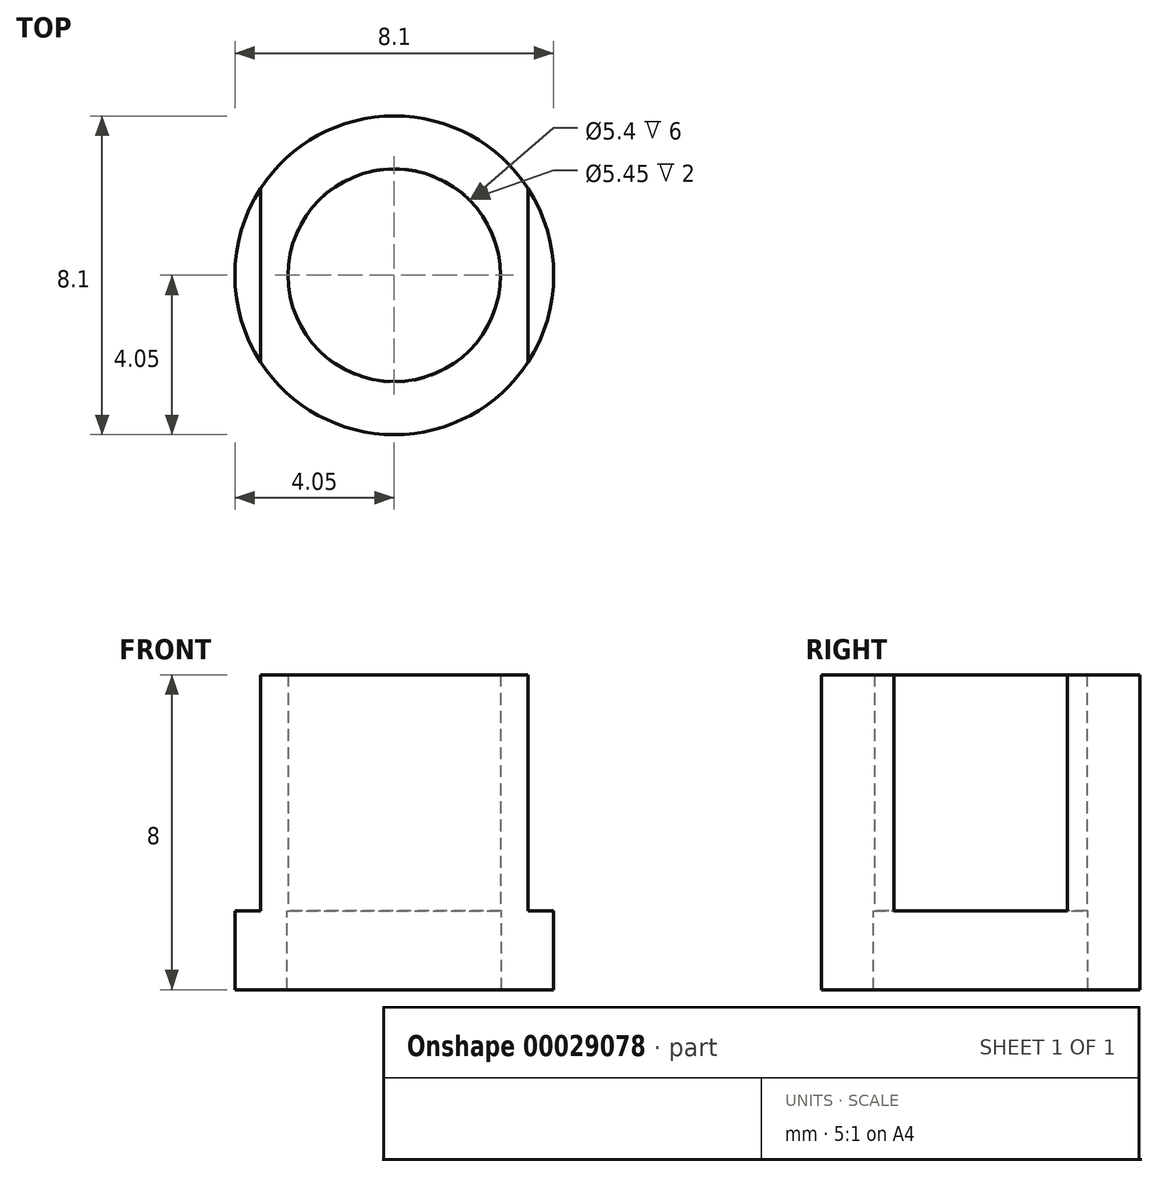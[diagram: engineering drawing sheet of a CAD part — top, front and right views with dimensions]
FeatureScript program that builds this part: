
annotation { "Feature Type Name" : "Feature", "Feature Type Description" : "" }
export const myFeature = defineFeature(function(context is Context, id is Id, definition is map)
    precondition{}
    {
        {
            var Q0;
            Q0=qCreatedBy(makeId("Top.planeOp"),FACE);
            var sketch = newSketch(context, id + "F0", { "sketchPlane" : qUnion([Q0])});
            skArc(sketch, "E0", {"start": v(3.4, 2.2) * mm, "mid": v(0, 4.05) * mm, "end": v(-3.4, 2.2) * mm});
            skCircle(sketch, "E1", {"center": v(0, 0) * mm, "radius": 2.7 * mm});
            skLineSegment(sketch, "E2", {"start": v(3.4, 2.2) * mm, "end": v(3.4, -2.2) * mm});
            skLineSegment(sketch, "E3.MirrorCS", {"start": v(-3.4, 2.2) * mm, "end": v(-3.4, -2.2) * mm});
            skArc(sketch, "E4.trimOffspring", {"start": v(-3.4, -2.2) * mm, "mid": v(0, -4.05) * mm, "end": v(3.4, -2.2) * mm});
            skSolve(sketch);
        }
        {
            var Q0;
            Q0=qSketchRegion(id+"F0",true);
            extrude(context, id + "F1", {"entities" : qUnion([Q0]), "depth" : 8 * mm});
        }
        {
            var Q0;
            Q0=makeQuery(id+"F1.opExtrude","CAP_FACE",FACE,{"disambiguationData":[OSD([sQuery(id+"F0.wireOp",EDGE,"E0"),sQuery(id+"F0.wireOp",EDGE,"E1"),sQuery(id+"F0.wireOp",EDGE,"E2"),sQuery(id+"F0.wireOp",EDGE,"E3.MirrorCS"),sQuery(id+"F0.wireOp",EDGE,"E4.trimOffspring")])],"isStart":true});
            var sketch = newSketch(context, id + "F2", { "sketchPlane" : qUnion([Q0])});
            skCircle(sketch, "E5", {"center": v(0, 0) * mm, "radius": 4.05 * mm});
            skSolve(sketch);
        }
        {
            var Q0;
            Q0=qSketchRegion(id+"F2",true);
            extrude(context, id + "F3", {"entities" : qUnion([Q0]), "operationType" : NewBodyOperationType.ADD, "oppositeDirection" : true, "depth" : 2 * mm});
        }
        {
            var Q0;
            Q0=makeQuery(id+"F3.opExtrude","CAP_FACE",FACE,{"disambiguationData":[OSD([sQuery(id+"F2.wireOp",EDGE,"E5")])],"isStart":false});
            var sketch = newSketch(context, id + "F4", { "sketchPlane" : qUnion([Q0])});
            skCircle(sketch, "E6", {"center": v(0, 0) * mm, "radius": 2.73 * mm});
            skSolve(sketch);
        }
        {
            var Q0;
            Q0=qSketchRegion(id+"F4",true);
            extrude(context, id + "F5", {"entities" : qUnion([Q0]), "operationType" : NewBodyOperationType.REMOVE, "endBound" : BoundingType.UP_TO_NEXT, "oppositeDirection" : true, "depth" : 25 * mm});
        }
    });
